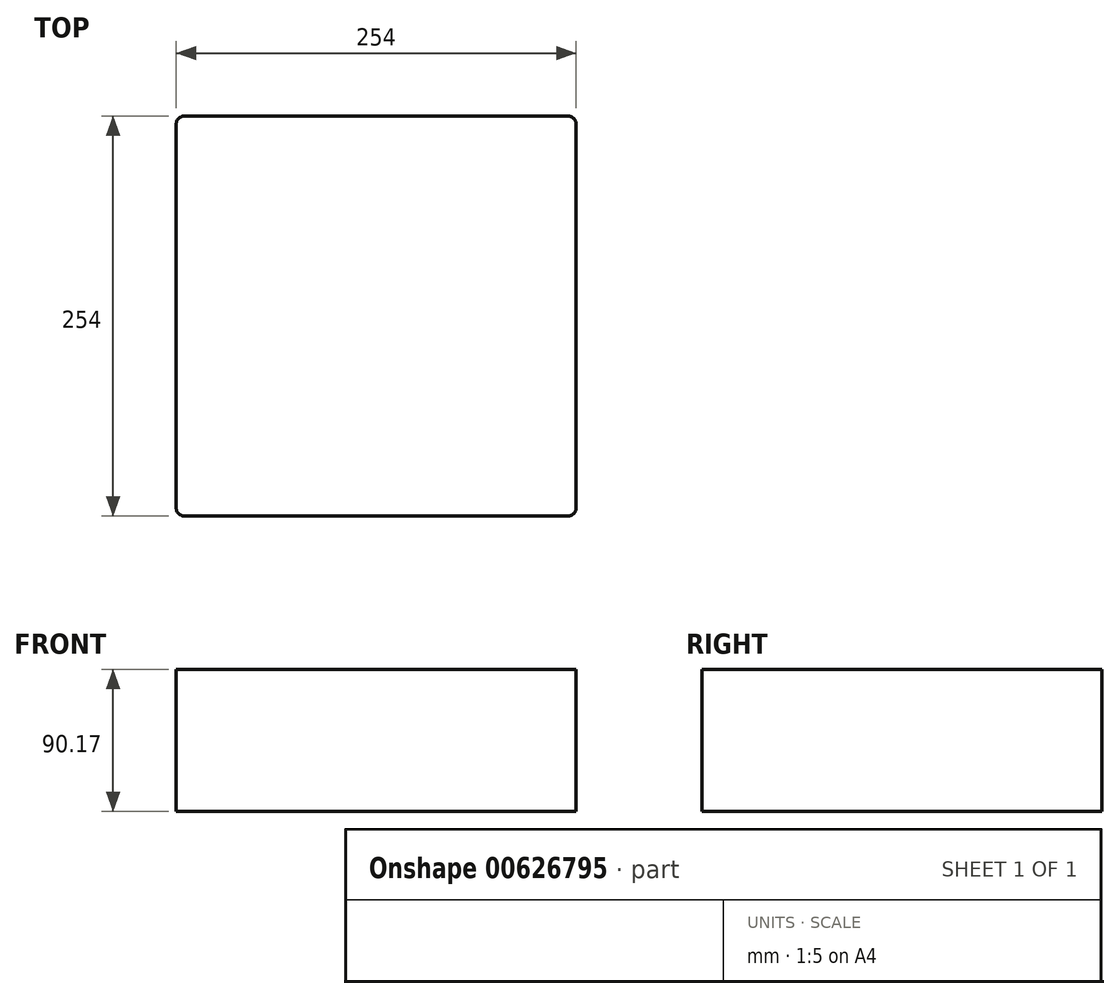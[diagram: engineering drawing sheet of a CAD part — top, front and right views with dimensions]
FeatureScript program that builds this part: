
annotation { "Feature Type Name" : "Feature", "Feature Type Description" : "" }
export const myFeature = defineFeature(function(context is Context, id is Id, definition is map)
    precondition{}
    {
        {
            var Q0;
            Q0=qCreatedBy(makeId("Top.planeOp"),FACE);
            var sketch = newSketch(context, id + "F0", { "sketchPlane" : qUnion([Q0])});
            skLineSegment(sketch, "E0.bottom", {"start": v(127, -127) * mm, "end": v(-127, -127) * mm});
            skLineSegment(sketch, "E0.top", {"start": v(127, 127) * mm, "end": v(-127, 127) * mm});
            skLineSegment(sketch, "E0.left", {"start": v(127, -127) * mm, "end": v(127, 127) * mm});
            skLineSegment(sketch, "E0.right", {"start": v(-127, -127) * mm, "end": v(-127, 127) * mm});
            skPoint(sketch, "E0.middle", {"position": v(0, 0) * mm});
            skSolve(sketch);
        }
        {
            var Q0;
            Q0=makeQuery(id+"F0.imprint","IMPRINT",FACE,{"disambiguationData":[TD([[makeQuery(id+"F0.imprint","IMPRINT",EDGE,{"derivedFrom":sQuery(id+"F0.wireOp",EDGE,"E0.bottom")}),-1.0]])]});
            extrude(context, id + "F1", {"entities" : qUnion([Q0]), "depth" : 90.17 * mm, "offsetDistance" : 25.4 * mm});
        }
        {
            var Q0;
            Q0=makeQuery(id+"F1.opExtrude","SWEPT_EDGE",EDGE,{"disambiguationData":[OSD([sQuery(id+"F0.wireOp",EDGE,"E0.top"),sQuery(id+"F0.wireOp",EDGE,"E0.left")])]});
            fillet(context, id + "F2", {"entities" : qUnion([Q0]), "radius" : 5.08 * mm, "tangentPropagation" : true, "allowEdgeOverflow" : false});
        }
        {
            var Q0;
            Q0=makeQuery(id+"F1.opExtrude","SWEPT_EDGE",EDGE,{"disambiguationData":[OSD([sQuery(id+"F0.wireOp",EDGE,"E0.top"),sQuery(id+"F0.wireOp",EDGE,"E0.right")])]});
            fillet(context, id + "F3", {"entities" : qUnion([Q0]), "radius" : 5.08 * mm, "tangentPropagation" : true, "allowEdgeOverflow" : false});
        }
        {
            var Q0;
            Q0=makeQuery(id+"F1.opExtrude","SWEPT_EDGE",EDGE,{"disambiguationData":[OSD([sQuery(id+"F0.wireOp",EDGE,"E0.bottom"),sQuery(id+"F0.wireOp",EDGE,"E0.right")])]});
            fillet(context, id + "F4", {"entities" : qUnion([Q0]), "radius" : 5.08 * mm, "tangentPropagation" : true, "allowEdgeOverflow" : false});
        }
        {
            var Q0;
            Q0=makeQuery(id+"F1.opExtrude","SWEPT_EDGE",EDGE,{"disambiguationData":[OSD([sQuery(id+"F0.wireOp",EDGE,"E0.bottom"),sQuery(id+"F0.wireOp",EDGE,"E0.left")])]});
            fillet(context, id + "F5", {"entities" : qUnion([Q0]), "radius" : 5.08 * mm, "tangentPropagation" : true, "allowEdgeOverflow" : false});
        }
    });
